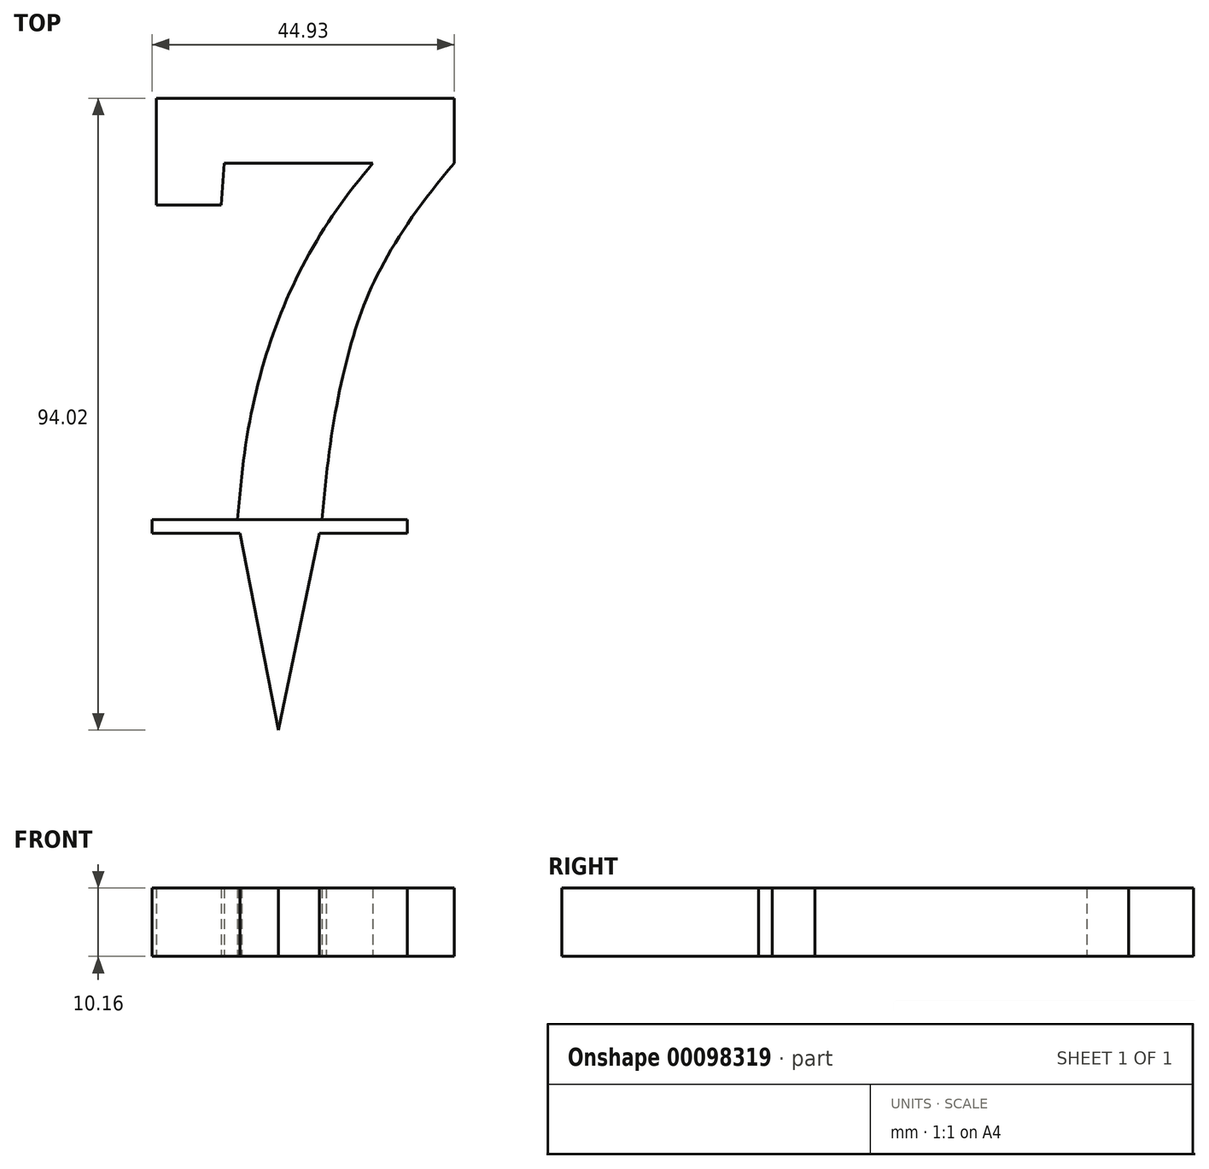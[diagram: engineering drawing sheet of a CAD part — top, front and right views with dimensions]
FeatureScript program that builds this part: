
annotation { "Feature Type Name" : "Feature", "Feature Type Description" : "" }
export const myFeature = defineFeature(function(context is Context, id is Id, definition is map)
    precondition{}
    {
        {
            var Q0;
            Q0=qCreatedBy(makeId("Top.planeOp"),FACE);
            var sketch = newSketch(context, id + "F0", { "sketchPlane" : qUnion([Q0])});
            skText(sketch, "E0", { "text": "7", "fontName": "RobotoSlab-Bold.ttf"});
            const initialGuessF0  = {"E0": [-0.02031, -0.034, 1, 0, 0.0635]};
            skSetInitialGuess(sketch, initialGuessF0);
            skSolve(sketch);
        }
        {
            var Q0;
            Q0 = qSketchRegion(id + "F0", true);
            extrude(context, id + "F1", {"entities" : qUnion([Q0]), "depth" : 10.16 * mm});
        }
        {
            var Q0;
            Q0=makeQuery(id+"F1.opExtrude","CAP_FACE",FACE,{"disambiguationData":[OSD([sQuery(id+"F0.wireOp",EDGE,"E0.sketch_text.stroke-0"),sQuery(id+"F0.wireOp",EDGE,"E0.sketch_text.stroke-1"),sQuery(id+"F0.wireOp",EDGE,"E0.sketch_text.stroke-2"),sQuery(id+"F0.wireOp",EDGE,"E0.sketch_text.stroke-3"),sQuery(id+"F0.wireOp",EDGE,"E0.sketch_text.stroke-4"),sQuery(id+"F0.wireOp",EDGE,"E0.sketch_text.stroke-5"),sQuery(id+"F0.wireOp",EDGE,"E0.sketch_text.stroke-6"),sQuery(id+"F0.wireOp",EDGE,"E0.sketch_text.stroke-7"),sQuery(id+"F0.wireOp",EDGE,"E0.sketch_text.stroke-8"),sQuery(id+"F0.wireOp",EDGE,"E0.sketch_text.stroke-9"),sQuery(id+"F0.wireOp",EDGE,"E0.sketch_text.stroke-10"),sQuery(id+"F0.wireOp",EDGE,"E0.sketch_text.stroke-11"),sQuery(id+"F0.wireOp",EDGE,"E0.sketch_text.stroke-12")])],"isStart":false});
            var sketch = newSketch(context, id + "F2", { "sketchPlane" : qUnion([Q0])});
            skLineSegment(sketch, "E1", {"start": v(-6.1, -34) * mm, "end": v(0, -65.32) * mm});
            skLineSegment(sketch, "E2", {"start": v(0, -65.32) * mm, "end": v(6.48, -34) * mm});
            skLineSegment(sketch, "E3", {"start": v(6.48, -34) * mm, "end": v(-6.1, -34) * mm});
            skSolve(sketch);
        }
        {
            var Q0;
            Q0 = qSketchRegion(id + "F2", true);
            var Q1;
            Q1=makeQuery(id+"F2.imprint","IMPRINT",FACE,{"disambiguationData":[TD([[makeQuery(id+"F2.imprint","IMPRINT",EDGE,{"derivedFrom":sQuery(id+"F2.wireOp",EDGE,"E1")}),1.0]])]});
            extrude(context, id + "F3", {"entities" : qUnion([Q0, Q1]), "operationType" : NewBodyOperationType.ADD, "oppositeDirection" : true, "depth" : 10.16 * mm});
        }
        {
            var Q0;
            Q0=makeQuery(id+"F3.boolean.opBoolean","MERGE",FACE,{"derivedFrom":[makeQuery(id+"F1.opExtrude","CAP_FACE",FACE,{"disambiguationData":[OSD([sQuery(id+"F0.wireOp",EDGE,"E0.sketch_text.stroke-0"),sQuery(id+"F0.wireOp",EDGE,"E0.sketch_text.stroke-1"),sQuery(id+"F0.wireOp",EDGE,"E0.sketch_text.stroke-2"),sQuery(id+"F0.wireOp",EDGE,"E0.sketch_text.stroke-3"),sQuery(id+"F0.wireOp",EDGE,"E0.sketch_text.stroke-4"),sQuery(id+"F0.wireOp",EDGE,"E0.sketch_text.stroke-5"),sQuery(id+"F0.wireOp",EDGE,"E0.sketch_text.stroke-6"),sQuery(id+"F0.wireOp",EDGE,"E0.sketch_text.stroke-7"),sQuery(id+"F0.wireOp",EDGE,"E0.sketch_text.stroke-8"),sQuery(id+"F0.wireOp",EDGE,"E0.sketch_text.stroke-9"),sQuery(id+"F0.wireOp",EDGE,"E0.sketch_text.stroke-10"),sQuery(id+"F0.wireOp",EDGE,"E0.sketch_text.stroke-11"),sQuery(id+"F0.wireOp",EDGE,"E0.sketch_text.stroke-12")])],"isStart":false}),makeQuery(id+"F3.opExtrude","CAP_FACE",FACE,{"disambiguationData":[OSD([sQuery(id+"F2.wireOp",EDGE,"E1"),sQuery(id+"F2.wireOp",EDGE,"E2"),sQuery(id+"F2.wireOp",EDGE,"E3")])],"isStart":true})]});
            var sketch = newSketch(context, id + "F4", { "sketchPlane" : qUnion([Q0])});
            skLineSegment(sketch, "E4", {"start": v(6.48, -34) * mm, "end": v(19.18, -34) * mm});
            skLineSegment(sketch, "E5", {"start": v(19.18, -34) * mm, "end": v(19.18, -36.04) * mm});
            skLineSegment(sketch, "E6", {"start": v(19.18, -36.04) * mm, "end": v(-18.8, -36.04) * mm});
            skLineSegment(sketch, "E7", {"start": v(-18.8, -36.04) * mm, "end": v(-18.8, -34) * mm});
            skLineSegment(sketch, "E8", {"start": v(-18.8, -34) * mm, "end": v(-6.1, -34) * mm});
            skLineSegment(sketch, "E9", {"start": v(-6.1, -34) * mm, "end": v(6.48, -34) * mm});
            skSolve(sketch);
        }
        {
            var Q0;
            {var subQ0=sQuery(id+"F4.wireOp",EDGE,"E4");Q0=makeQuery(id+"F4.imprint","IMPRINT",FACE,{"disambiguationData":[TD([[makeQuery(id+"F4.imprint","IMPRINT",EDGE,{"derivedFrom":subQ0}),-1.0]])]});}
            var Q1;
            {var subQ0=sQuery(id+"F4.wireOp",EDGE,"E7");Q1=makeQuery(id+"F4.imprint","IMPRINT",FACE,{"disambiguationData":[TD([[makeQuery(id+"F4.imprint","IMPRINT",EDGE,{"derivedFrom":subQ0}),-1.0]])]});}
            extrude(context, id + "F5", {"entities" : qUnion([Q0, Q1]), "operationType" : NewBodyOperationType.ADD, "oppositeDirection" : true, "depth" : 10.16 * mm});
        }
    });
